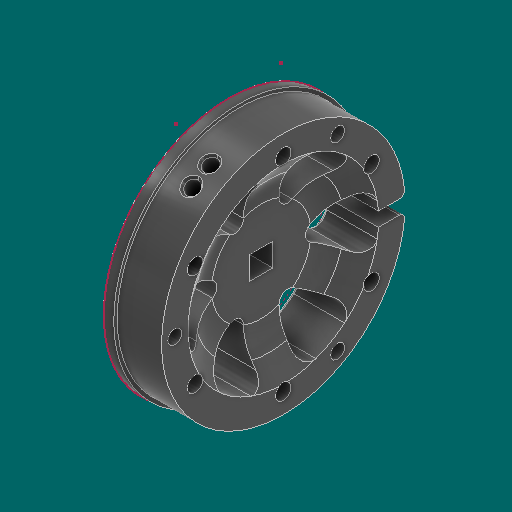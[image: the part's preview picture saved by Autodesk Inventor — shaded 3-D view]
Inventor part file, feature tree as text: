
AUTODESK INVENTOR PART (.ipt)
format: ipt  version: 2023.1 (Build 271208000, 208)  size: 566,272 bytes
history: native  units: in
note: dims shown in document units (in); Inventor stores cm internally (conversion verified against a paired STEP export)
features: sketch x5, other x3
ambient origin geometry x8: Origin, YZ Plane, XZ Plane, XY Plane, X Axis, Y Axis, Z Axis, Center Point
bodies: Solid1 (feature_tree)
feature tree (8):
  other  "WheelHalf_MIR_MIR.ipt"
  other  "Solid1::WheelHalf_MIR_MIR.ipt"
  other  "TaggingFeature1"
  sketch  "Sketch1"  dims[d0=0.3937in]
  sketch  "Sketch2"
  sketch  "Sketch3"
  sketch  "Sketch4"
  sketch  "Sketch5"
